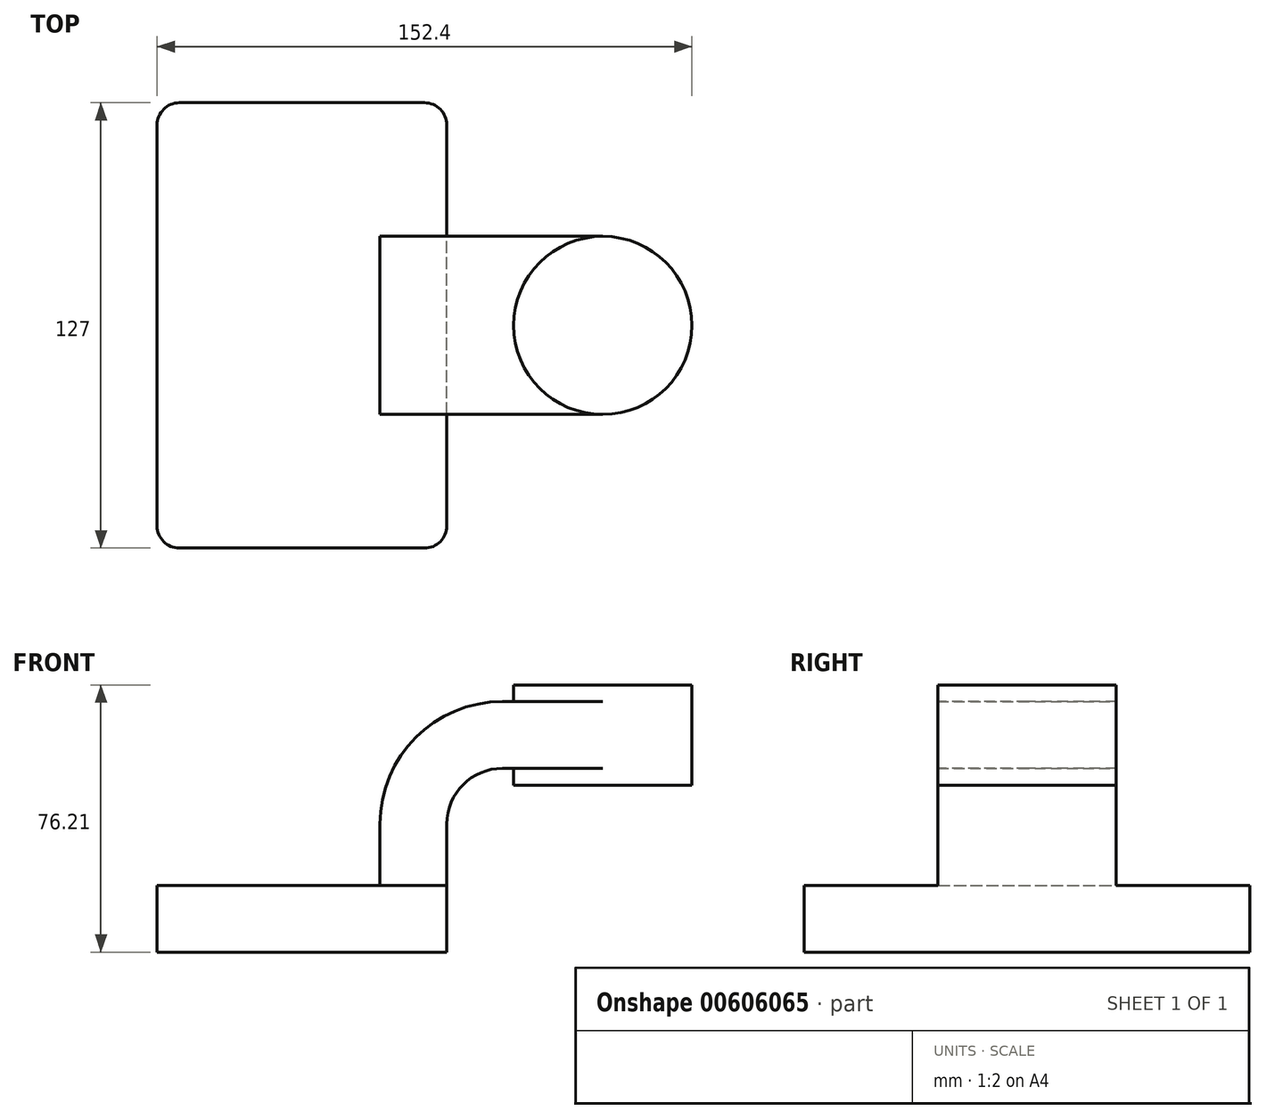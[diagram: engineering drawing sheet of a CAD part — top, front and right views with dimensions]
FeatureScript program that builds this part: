
annotation { "Feature Type Name" : "Feature", "Feature Type Description" : "" }
export const myFeature = defineFeature(function(context is Context, id is Id, definition is map)
    precondition{}
    {
        {
            var Q0;
            Q0=qCreatedBy(makeId("Front.planeOp"),FACE);
            var sketch = newSketch(context, id + "F0", { "sketchPlane" : qUnion([Q0])});
            skLineSegment(sketch, "E0.bottom", {"start": v(41.27, 9.53) * mm, "end": v(-41.28, 9.53) * mm});
            skLineSegment(sketch, "E0.top", {"start": v(41.28, -9.52) * mm, "end": v(-41.27, -9.52) * mm});
            skLineSegment(sketch, "E0.left", {"start": v(41.28, 9.53) * mm, "end": v(41.28, -9.52) * mm});
            skLineSegment(sketch, "E0.right", {"start": v(-41.28, 9.53) * mm, "end": v(-41.27, -9.52) * mm});
            skPoint(sketch, "E0.middle", {"position": v(0, 0) * mm});
            skLineSegment(sketch, "E1", {"start": v(41.27, 9.53) * mm, "end": v(41.27, 27) * mm});
            skArc(sketch, "E2", {"start": v(41.28, 27) * mm, "mid": v(45.92, 38.23) * mm, "end": v(57.15, 42.88) * mm});
            skLineSegment(sketch, "E3.bottom", {"start": v(60.33, 38.1) * mm, "end": v(111.13, 38.1) * mm});
            skLineSegment(sketch, "E3.top", {"start": v(60.33, 66.68) * mm, "end": v(111.13, 66.68) * mm});
            skLineSegment(sketch, "E3.left", {"start": v(60.33, 38.1) * mm, "end": v(60.33, 66.68) * mm});
            skLineSegment(sketch, "E3.right", {"start": v(111.13, 38.1) * mm, "end": v(111.13, 66.68) * mm});
            skPoint(sketch, "E3.middle", {"position": v(85.73, 52.39) * mm});
            skLineSegment(sketch, "E4", {"start": v(57.15, 42.88) * mm, "end": v(85.73, 42.88) * mm});
            skLineSegment(sketch, "E5.0", {"start": v(57.15, 61.93) * mm, "end": v(85.73, 61.93) * mm});
            skArc(sketch, "E5.1", {"start": v(22.23, 27) * mm, "mid": v(32.45, 51.7) * mm, "end": v(57.15, 61.93) * mm});
            skLineSegment(sketch, "E5.2", {"start": v(22.22, 9.53) * mm, "end": v(22.22, 27) * mm});
            skLineSegment(sketch, "E6", {"start": v(85.73, 38.1) * mm, "end": v(85.73, 66.68) * mm});
            skFitSpline(sketch, "E7", {"points": [v(-41.28, 9.53) * mm, v(57.15, 61.93) * mm], "startDerivative": vector(0, 86.08) * mm, "endDerivative": vector(171.45, 0) * mm});
            skSolve(sketch);
        }
        {
            var Q0;
            Q0=makeQuery(id+"F0.imprint","IMPRINT",FACE,{"disambiguationData":[TD([[makeQuery(id+"F0.imprint","IMPRINT",EDGE,{"derivedFrom":sQuery(id+"F0.wireOp",EDGE,"E0.top")}),-1.0]])]});
            extrude(context, id + "F1", {"entities" : qUnion([Q0]), "endBound" : BoundingType.SYMMETRIC, "depth" : 127 * mm, "offsetDistance" : 25.4 * mm});
        }
        {
            var Q0;
            {var subQ7=sQuery(id+"F0.wireOp",EDGE,"E1");Q0=makeQuery(id+"F0.imprint","IMPRINT",FACE,{"disambiguationData":[TD([[makeQuery(id+"F0.imprint","IMPRINT",EDGE,{"derivedFrom":subQ7}),1.0]])]});}
            var Q1;
            {var subQ0=sQuery(id+"F0.wireOp",EDGE,"E4");var subQ1=sQuery(id+"F0.wireOp",EDGE,"E3.left");var subQ2=makeQuery(id+"F0.imprint","INTERSECT",VERTEX,{"derivedFrom":[subQ1,subQ0]});Q1=makeQuery(id+"F0.imprint","IMPRINT",FACE,{"disambiguationData":[TD([[makeQuery(id+"F0.imprint","IMPRINT",EDGE,{"disambiguationData":[TD([[subQ2,-1.0]])],"derivedFrom":subQ1}),-1.0]])]});}
            extrude(context, id + "F2", {"entities" : qUnion([Q0, Q1]), "operationType" : NewBodyOperationType.ADD, "endBound" : BoundingType.SYMMETRIC, "depth" : 50.8 * mm, "offsetDistance" : 25.4 * mm});
        }
        {
            var Q0;
            Q0=makeQuery(id+"F0.imprint","IMPRINT",FACE,{"disambiguationData":[TD([[makeQuery(id+"F0.imprint","IMPRINT",EDGE,{"derivedFrom":sQuery(id+"F0.wireOp",EDGE,"E5.1")}),1.0]])]});
            extrude(context, id + "F3", {"entities" : qUnion([Q0]), "operationType" : NewBodyOperationType.ADD, "endBound" : BoundingType.SYMMETRIC, "depth" : 15.88 * mm, "offsetDistance" : 25.4 * mm});
        }
        {
            var Q0;
            {var subQ4=sQuery(id+"F0.wireOp",EDGE,"E3.right");Q0=makeQuery(id+"F0.imprint","IMPRINT",FACE,{"disambiguationData":[TD([[makeQuery(id+"F0.imprint","IMPRINT",EDGE,{"derivedFrom":subQ4}),1.0]])]});}
            var Q1;
            Q1=sQuery(id+"F0.wireOp",EDGE,"E6");
            revolve(context, id + "F4", {"operationType" : NewBodyOperationType.ADD, "entities" : qUnion([Q0]), "axis" : qUnion([Q1]), "revolveType" : RevolveType.FULL});
        }
        {
            var Q0;
            Q0=makeQuery(id+"F1.opExtrude","CAP_EDGE",EDGE,{"disambiguationData":[OSD([sQuery(id+"F0.wireOp",EDGE,"E0.left")])],"isStart":false});
            var Q1;
            Q1=makeQuery(id+"F1.opExtrude","CAP_EDGE",EDGE,{"disambiguationData":[OSD([sQuery(id+"F0.wireOp",EDGE,"E0.right")])],"isStart":false});
            var Q2;
            Q2=makeQuery(id+"F1.opExtrude","CAP_EDGE",EDGE,{"disambiguationData":[OSD([sQuery(id+"F0.wireOp",EDGE,"E0.right")])],"isStart":true});
            var Q3;
            Q3=makeQuery(id+"F1.opExtrude","CAP_EDGE",EDGE,{"disambiguationData":[OSD([sQuery(id+"F0.wireOp",EDGE,"E0.left")])],"isStart":true});
            fillet(context, id + "F5", {"entities" : qUnion([Q0, Q1, Q2, Q3]), "radius" : 6.35 * mm, "tangentPropagation" : true, "allowEdgeOverflow" : false});
        }
    });
